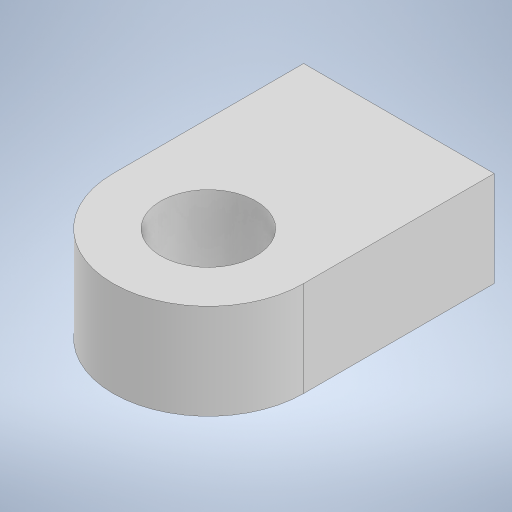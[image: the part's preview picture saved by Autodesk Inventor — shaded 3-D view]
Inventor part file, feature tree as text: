
AUTODESK INVENTOR PART (.ipt)
format: ipt  version: 2023 (Build 270158000, 158)  size: 196,608 bytes
history: native  units: mm
features: extrude x1, sketch x1
ambient origin geometry x8: Origin, YZ Plane, XZ Plane, XY Plane, X Axis, Y Axis, Z Axis, Center Point
bodies: Solido1 (feature_tree)
feature tree (2):
  extrude  "Estrusione1"  Depth=10.0mm
  sketch  "Schizzo2"
